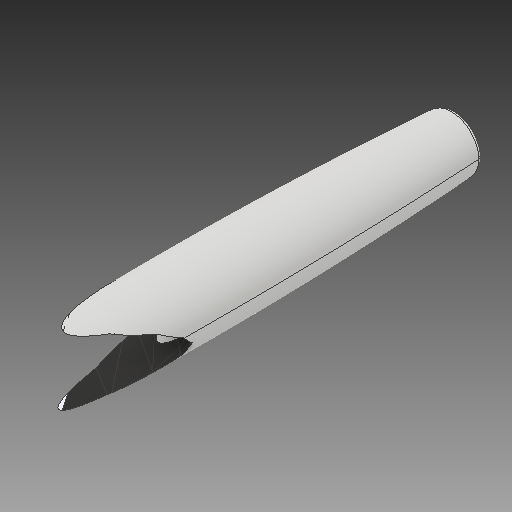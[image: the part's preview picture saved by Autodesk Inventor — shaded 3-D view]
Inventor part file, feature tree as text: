
AUTODESK INVENTOR PART (.ipt)
format: ipt  version: 2017 (Build 210142000, 142)  size: 342,016 bytes
history: native  units: in
note: dims shown in document units (in); Inventor stores cm internally (conversion verified against a paired STEP export)
features: sketch x6, other x5, plane x2
ambient origin geometry x8: Origin, YZ Plane, XZ Plane, XY Plane, X Axis, Y Axis, Z Axis, Center Point
bodies: Solid1 (feature_tree), Solid2 (feature_tree)
feature tree (13):
  other  "Part2.ipt"
  other  "Solid2::Part2.ipt"
  other  "Solid5::Part2.ipt"
  other  "Solid6::Part2.ipt"
  other  "TaggingFeature1"
  sketch  "Sketch5"  dims[d0=0.3937in]
  sketch  "Sketch6"
  sketch  "Sketch7"
  sketch  "Sketch9"
  sketch  "Sketch14"
  sketch  "Sketch17"
  plane  "Work Plane9"
  plane  "Work Plane10"
